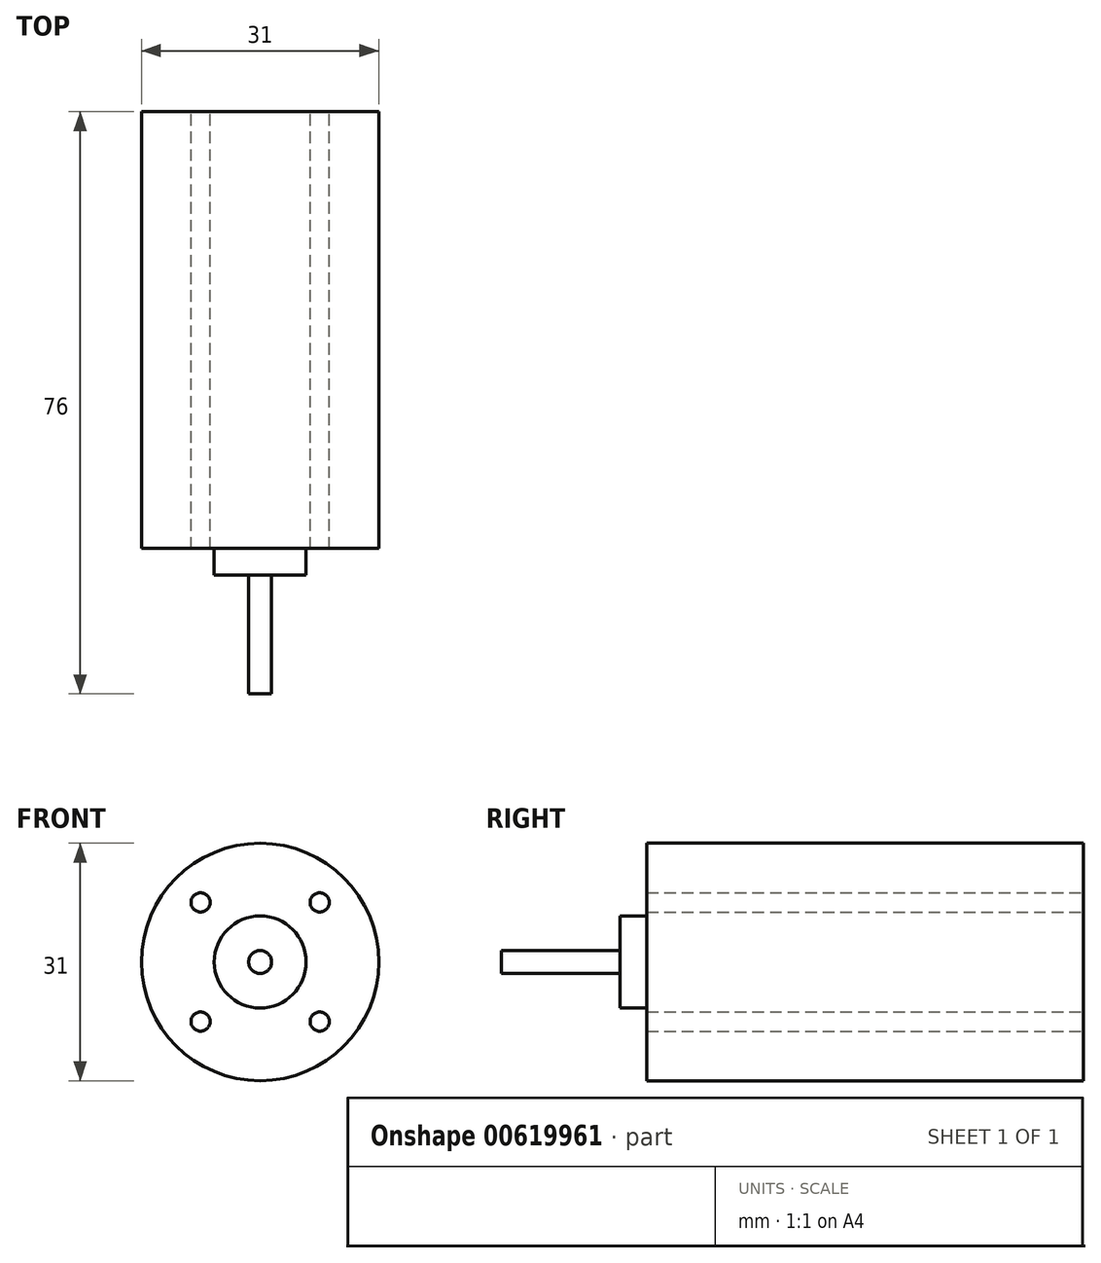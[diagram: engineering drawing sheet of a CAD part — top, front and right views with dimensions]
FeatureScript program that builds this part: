
annotation { "Feature Type Name" : "Feature", "Feature Type Description" : "" }
export const myFeature = defineFeature(function(context is Context, id is Id, definition is map)
    precondition{}
    {
        {
            var Q0;
            Q0=qCreatedBy(makeId("Front.planeOp"),FACE);
            var sketch = newSketch(context, id + "F0", { "sketchPlane" : qUnion([Q0])});
            skCircle(sketch, "E0", {"center": v(0, 0) * mm, "radius": 15.5 * mm});
            skSolve(sketch);
        }
        {
            var Q0;
            Q0=makeQuery(id+"F0.imprint","IMPRINT",FACE,{"disambiguationData":[TD([[makeQuery(id+"F0.imprint","IMPRINT",EDGE,{"derivedFrom":sQuery(id+"F0.wireOp",EDGE,"E0")}),1.0]])]});
            extrude(context, id + "F1", {"entities" : qUnion([Q0]), "depth" : 57 * mm, "offsetDistance" : 25 * mm});
        }
        {
            var Q0;
            Q0=makeQuery(id+"F1.opExtrude","CAP_FACE",FACE,{"disambiguationData":[OSD([sQuery(id+"F0.wireOp",EDGE,"E0")])],"isStart":false});
            var sketch = newSketch(context, id + "F2", { "sketchPlane" : qUnion([Q0])});
            skCircle(sketch, "E1", {"center": v(0, 0) * mm, "radius": 6 * mm});
            skPoint(sketch, "E2", {"position": v(-7.78, 7.78) * mm});
            skPoint(sketch, "E3.MirrorP", {"position": v(7.78, 7.78) * mm});
            skPoint(sketch, "E4.MirrorP", {"position": v(7.78, -7.78) * mm});
            skPoint(sketch, "E5.MirrorP", {"position": v(-7.78, -7.78) * mm});
            skSolve(sketch);
        }
        {
            var Q0;
            Q0 = qSketchRegion(id + "F2", true);
            extrude(context, id + "F3", {"entities" : qUnion([Q0]), "operationType" : NewBodyOperationType.ADD, "depth" : 3.5 * mm, "offsetDistance" : 25 * mm});
        }
        {
            var Q0;
            Q0=makeQuery(id+"F3.opExtrude","CAP_FACE",FACE,{"disambiguationData":[OSD([sQuery(id+"F2.wireOp",EDGE,"E1")])],"isStart":false});
            var sketch = newSketch(context, id + "F4", { "sketchPlane" : qUnion([Q0])});
            skCircle(sketch, "E6", {"center": v(0, 0) * mm, "radius": 1.5 * mm});
            skSolve(sketch);
        }
        {
            var Q0;
            Q0 = qSketchRegion(id + "F4", true);
            extrude(context, id + "F5", {"entities" : qUnion([Q0]), "operationType" : NewBodyOperationType.ADD, "depth" : 15.5 * mm, "offsetDistance" : 25 * mm});
        }
        {
            var Q0;
            Q0=sQuery(id+"F2.wireOp",VERTEX,"E2");
            var Q1;
            Q1=sQuery(id+"F2.wireOp",VERTEX,"E3.MirrorP");
            var Q2;
            Q2=sQuery(id+"F2.wireOp",VERTEX,"E4.MirrorP");
            var Q3;
            Q3=sQuery(id+"F2.wireOp",VERTEX,"E5.MirrorP");
            var Q4;
            Q4=makeQuery(id+"F1.opExtrude","SWEPT_BODY",BODY,{"disambiguationData":[OSD([sQuery(id+"F0.wireOp",EDGE,"E0")])]});
            hole(context, id + "F6", {"style" : HoleStyle.SIMPLE, "endStyle" : HoleEndStyle.THROUGH, "standardTappedOrClearance" : lookupTablePath({ "standard" : "ISO", "engagement" : "75%", "pitch" : "0.5 mm", "size" : "M3", "type" : "Tapped" }), "standardBlindInLast" : lookupTablePath({ "standard" : "ISO", "engagement" : "75%", "pitch" : "0.5 mm", "size" : "M3", "type" : "Tapped" }), "holeDiameter" : 2.5 * mm, "majorDiameter" : 3 * mm, "showTappedDepth" : true, "isTappedThrough" : true, "tappedDepth" : 21 * mm, "tapClearance" : 0, "locations" : qUnion([Q0, Q1, Q2, Q3]), "scope" : qUnion([Q4]), "startStyle" : HoleStartStyle.SKETCH});
        }
    });
